# Revit family: Electronics_Visual-Projectors_ViewSonic_The-ViewSonicR-LS830-Projectors
name_source: partatom
category: Electrical Equipment
revit_build: Autodesk Revit 2015 (Build: 20140606_1530(x64)
units: mm (PartAtom-declared; Revit-internal decimal feet)

## types (1)
- LS830
    Assembly Code = D50
    BIMobject category = Visual - Projectors
    BIMobject category code = electronics-visual-projectors
    BIMobject main category = Electronics
    BIMobject main category code = electronics
    BOSUseNativeGeometries = 1
    Brand url = https://www.viewsonic.com
    Covering Color = Plastic - Viewsonic - Black
    Description = Featuring stunning 1080p resolution and 4,500 lumens of brightness, the ViewSonic® LS830 Laser Projector is the ideal solution for modern business and education environments. Designed with a laser phosphor light source lasting up to 20,000 hours, this projector delivers long-term, virtually maintenance-free usage for any boardroom or classroom. With its 0.23 ultra-short throw ratio, HV keystoning and 4 corner adjustments, the LS830 makes installation a hassle-free experience. What’s more, the ultra-short throw ratio allows you to place the projector just inches away from a wall or screen to give you a huge image for less cost than a comparably sized display. The LS830 also features a hidden PortAll® compartment which accommodates additional accessories such as a wireless streaming device, or PC stick. Powered by SuperColor technology for true-to-life images, and SonicExpert® technology for incredibly clear sound, the LS830 delivers an immersive audiovisual performance.
    Design country = Taiwan
    Edition number = 1
    Keynote = V90
    Manufacturer = ViewSonic
    Manufacturer country = Taiwan
    Manufacturer name = ViewSonic
    Model = viewsonic_ls830
    Product Guid = db851024-411a-4c3f-a924-c8e52ebc0721
    Product SKU = viewsonic_ls830
    Product data url = https://bimobject.com
    Product family = Electronics
    Product group = Projectors
    Product name = The ViewSonic® LS830 Projector
    Product url = https://www.viewsonic.com
    Projection Angle = 25.00°
    QR code = http://bimobject.com
    URL = www.viewsonic.com
    a = Image Aspect Ratio : "4  - 3"
    b = Image Aspect Ratio : "16 - 9"
    c = Image Aspect Ratio : "16 - 10"

## geometry (parser evidence)
native form markers: Blend x2, Sweep x6
no freeform markers — native parametric forms only
